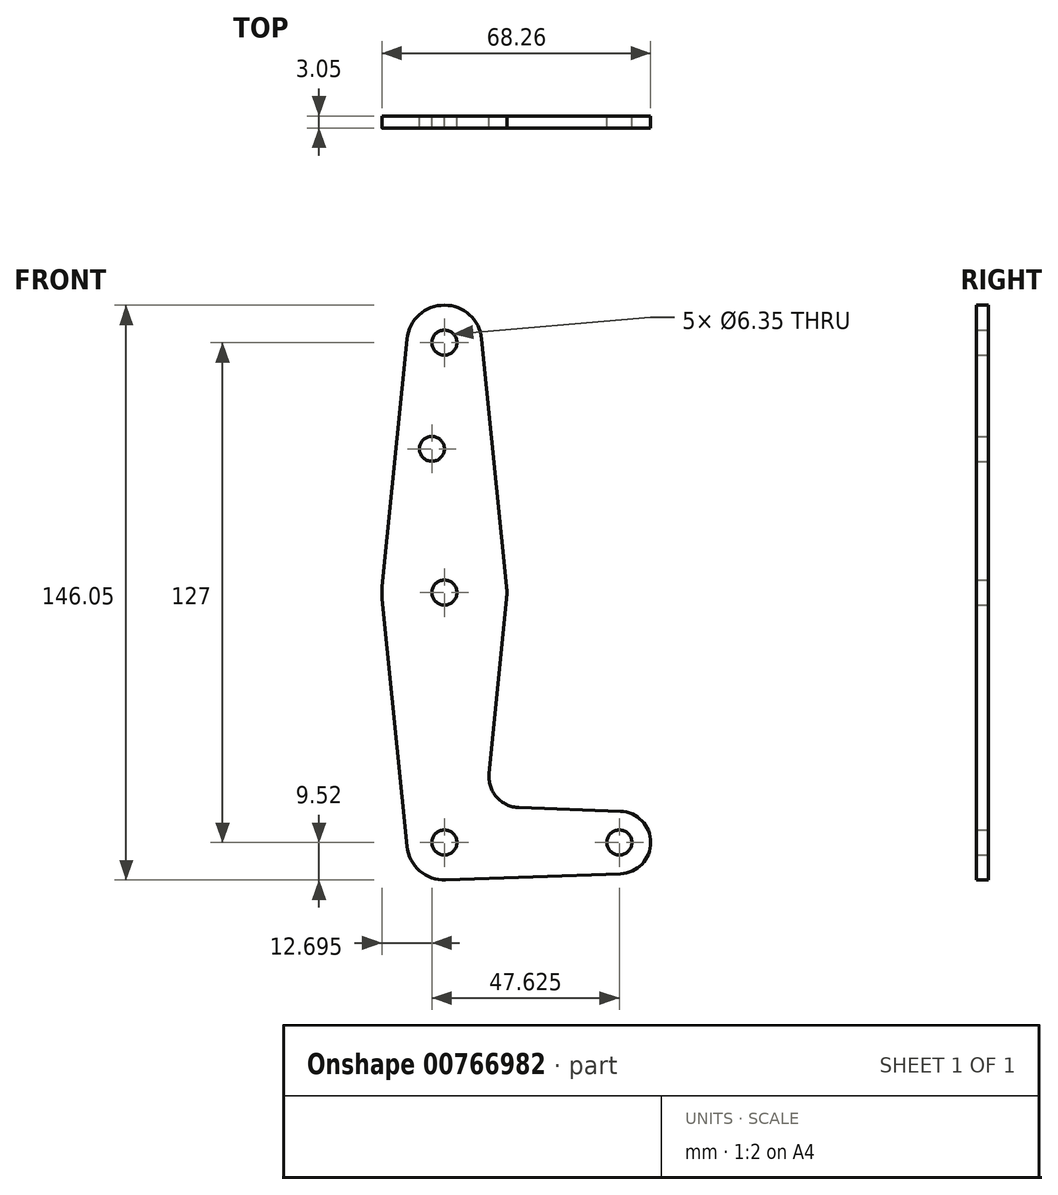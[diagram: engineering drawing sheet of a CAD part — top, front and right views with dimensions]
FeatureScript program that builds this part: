
annotation { "Feature Type Name" : "Feature", "Feature Type Description" : "" }
export const myFeature = defineFeature(function(context is Context, id is Id, definition is map)
    precondition{}
    {
        {
            var Q0;
            Q0=qCreatedBy(makeId("Front.planeOp"),FACE);
            var sketch = newSketch(context, id + "F0", { "sketchPlane" : qUnion([Q0])});
            skCircle(sketch, "E0", {"center": v(0, 0) * mm, "radius": 9.53 * mm});
            skCircle(sketch, "E1", {"center": v(44.45, 0) * mm, "radius": 7.94 * mm});
            skCircle(sketch, "E2", {"center": v(0, 63.5) * mm, "radius": 15.88 * mm});
            skCircle(sketch, "E3", {"center": v(0, 127) * mm, "radius": 9.53 * mm});
            skLineSegment(sketch, "E4", {"start": v(0, 127) * mm, "end": v(0, 0) * mm, "construction": true});
            skLineSegment(sketch, "E5", {"start": v(0, 0) * mm, "end": v(44.45, 0) * mm, "construction": true});
            skLineSegment(sketch, "E6", {"start": v(-9.48, 127.95) * mm, "end": v(-15.8, 65.09) * mm});
            skLineSegment(sketch, "E7", {"start": v(-15.8, 61.91) * mm, "end": v(-9.48, -0.95) * mm});
            skLineSegment(sketch, "E8", {"start": v(11.34, 17.6) * mm, "end": v(15.8, 61.91) * mm});
            skLineSegment(sketch, "E9", {"start": v(15.8, 65.09) * mm, "end": v(9.48, 127.95) * mm});
            skLineSegment(sketch, "E10", {"start": v(18.97, 8.85) * mm, "end": v(44.73, 7.93) * mm});
            skLineSegment(sketch, "E11", {"start": v(44.73, -7.93) * mm, "end": v(0.34, -9.52) * mm});
            skCircle(sketch, "E12", {"center": v(0, 127) * mm, "radius": 3.18 * mm});
            skCircle(sketch, "E13", {"center": v(-3.18, 100.03) * mm, "radius": 3.18 * mm});
            skCircle(sketch, "E14", {"center": v(0, 63.5) * mm, "radius": 3.18 * mm});
            skCircle(sketch, "E15", {"center": v(0, 0) * mm, "radius": 3.18 * mm});
            skCircle(sketch, "E16", {"center": v(44.45, 0) * mm, "radius": 3.18 * mm});
            skArc(sketch, "E17.filletArc", {"start": v(11.34, 17.6) * mm, "mid": v(13.26, 11.57) * mm, "end": v(18.97, 8.85) * mm});
            skSolve(sketch);
        }
        {
            var Q0;
            Q0 = qSketchRegion(id + "F0", true);
            extrude(context, id + "F1", {"entities" : qUnion([Q0]), "depth" : 3.05 * mm, "offsetDistance" : 25.4 * mm});
        }
    });
